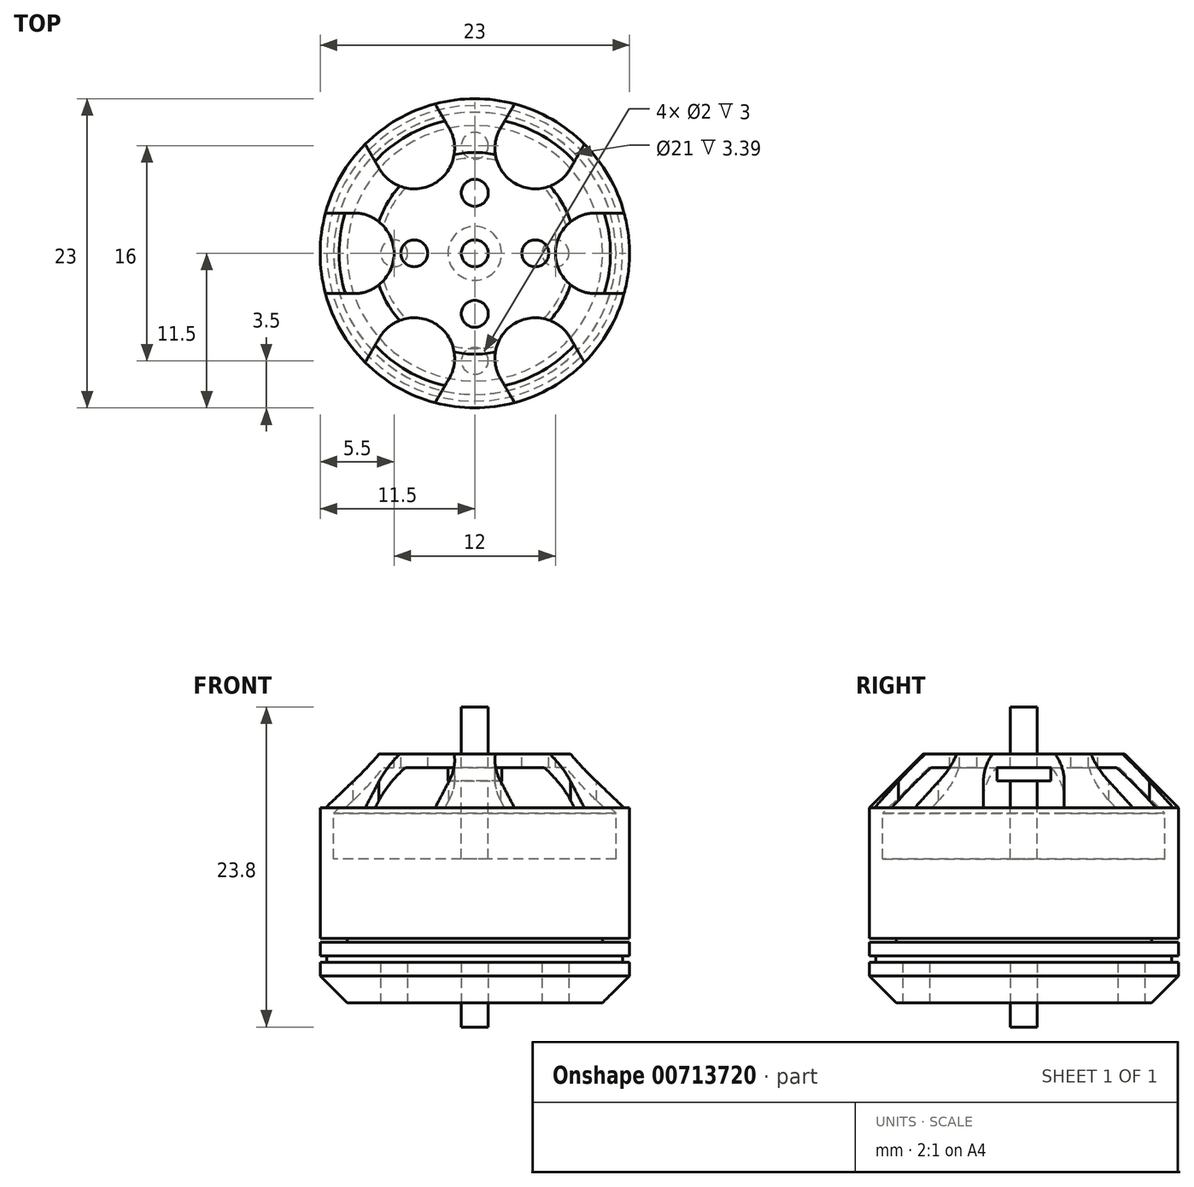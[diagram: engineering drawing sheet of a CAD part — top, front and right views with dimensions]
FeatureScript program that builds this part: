
annotation { "Feature Type Name" : "Feature", "Feature Type Description" : "" }
export const myFeature = defineFeature(function(context is Context, id is Id, definition is map)
    precondition{}
    {
        {
            var Q0;
            Q0=qCreatedBy(makeId("Front.planeOp"),FACE);
            var sketch = newSketch(context, id + "F0", { "sketchPlane" : qUnion([Q0])});
            skLineSegment(sketch, "E0", {"start": v(0, 22) * mm, "end": v(0, 0) * mm});
            skLineSegment(sketch, "E1", {"start": v(1, 0) * mm, "end": v(9.5, 0) * mm});
            skLineSegment(sketch, "E2", {"start": v(9.5, 0) * mm, "end": v(11.5, 2) * mm});
            skLineSegment(sketch, "E3", {"start": v(11.5, 2) * mm, "end": v(11.5, 3) * mm});
            skLineSegment(sketch, "E4", {"start": v(11.5, 14.5) * mm, "end": v(7.5, 18.5) * mm});
            skLineSegment(sketch, "E5", {"start": v(7.5, 18.5) * mm, "end": v(1, 18.5) * mm});
            skLineSegment(sketch, "E6", {"start": v(1, 18.5) * mm, "end": v(1, 22) * mm});
            skLineSegment(sketch, "E7", {"start": v(1, 22) * mm, "end": v(0, 22) * mm});
            skLineSegment(sketch, "E8", {"start": v(0, 0) * mm, "end": v(0, -1.8) * mm});
            skLineSegment(sketch, "E9", {"start": v(0, -1.8) * mm, "end": v(1, -1.8) * mm});
            skLineSegment(sketch, "E10", {"start": v(1, -1.8) * mm, "end": v(1, 0) * mm});
            skLineSegment(sketch, "E11", {"start": v(2, 17.5) * mm, "end": v(7.09, 17.5) * mm});
            skLineSegment(sketch, "E12", {"start": v(7.09, 17.5) * mm, "end": v(10.5, 14.09) * mm});
            skLineSegment(sketch, "E13", {"start": v(10.5, 14.09) * mm, "end": v(10.5, 10.7) * mm});
            skLineSegment(sketch, "E14", {"start": v(10.5, 10.7) * mm, "end": v(1, 10.7) * mm});
            skLineSegment(sketch, "E15", {"start": v(1, 10.7) * mm, "end": v(1, 16.5) * mm});
            skLineSegment(sketch, "E16", {"start": v(1, 16.5) * mm, "end": v(2, 16.5) * mm});
            skLineSegment(sketch, "E17", {"start": v(2, 16.5) * mm, "end": v(2, 17.5) * mm});
            skLineSegment(sketch, "E18", {"start": v(11.5, 3) * mm, "end": v(11, 3) * mm});
            skLineSegment(sketch, "E19", {"start": v(11, 3) * mm, "end": v(11, 3.5) * mm});
            skLineSegment(sketch, "E20", {"start": v(11, 3.5) * mm, "end": v(11.5, 3.5) * mm});
            skLineSegment(sketch, "E21", {"start": v(11.5, 4.5) * mm, "end": v(9.5, 4.5) * mm});
            skLineSegment(sketch, "E22", {"start": v(9.5, 4.5) * mm, "end": v(9.5, 4.8) * mm});
            skLineSegment(sketch, "E23", {"start": v(9.5, 4.8) * mm, "end": v(11.5, 4.8) * mm});
            skLineSegment(sketch, "E24.trimOffspring", {"start": v(11.5, 3.5) * mm, "end": v(11.5, 4.5) * mm});
            skLineSegment(sketch, "E25.trimOffspring", {"start": v(11.5, 4.8) * mm, "end": v(11.5, 14.5) * mm});
            skSolve(sketch);
        }
        {
            var Q0;
            Q0=makeQuery(id+"F0.imprint","IMPRINT",FACE,{"disambiguationData":[TD([[makeQuery(id+"F0.imprint","IMPRINT",EDGE,{"derivedFrom":sQuery(id+"F0.wireOp",EDGE,"E0")}),1.0]])]});
            var Q1;
            Q1=sQuery(id+"F0.wireOp",EDGE,"E0");
            revolve(context, id + "F1", {"entities" : qUnion([Q0]), "axis" : qUnion([Q1]), "revolveType" : RevolveType.FULL});
        }
        {
            var Q0;
            Q0=makeQuery(id+"F1.opRevolve","SWEPT_FACE",FACE,{"disambiguationData":[OSD([sQuery(id+"F0.wireOp",EDGE,"E5")])]});
            var sketch = newSketch(context, id + "F2", { "sketchPlane" : qUnion([Q0])});
            skCircle(sketch, "E26", {"center": v(0, 0) * mm, "radius": 4.5 * mm, "construction": true});
            skLineSegment(sketch, "E27", {"start": v(0, 0) * mm, "end": v(-9, 0) * mm, "construction": true});
            skCircle(sketch, "E28", {"center": v(4.5, 0) * mm, "radius": 1 * mm});
            skCircle(sketch, "E29.1.0", {"center": v(0, 4.5) * mm, "radius": 1 * mm});
            skCircle(sketch, "E29.2.0", {"center": v(-4.5, 0) * mm, "radius": 1 * mm});
            skCircle(sketch, "E29.3.0", {"center": v(0, -4.5) * mm, "radius": 1 * mm});
            skArc(sketch, "E30", {"start": v(-9.05, -3) * mm, "mid": v(-6, 0) * mm, "end": v(-9.05, 3) * mm});
            skLineSegment(sketch, "E31", {"start": v(-8.95, -3) * mm, "end": v(-15.53, -3) * mm});
            skLineSegment(sketch, "E32", {"start": v(-15.53, -3) * mm, "end": v(-15.53, 3) * mm});
            skLineSegment(sketch, "E33", {"start": v(-15.53, 3) * mm, "end": v(-8.95, 3) * mm});
            skLineSegment(sketch, "E34.1.0", {"start": v(-5.17, -14.95) * mm, "end": v(-10.36, -11.95) * mm});
            skLineSegment(sketch, "E34.1.1", {"start": v(-1.88, -9.25) * mm, "end": v(-5.17, -14.95) * mm});
            skArc(sketch, "E34.1.2", {"start": v(-1.93, -9.34) * mm, "mid": v(-3, -5.2) * mm, "end": v(-7.12, -6.34) * mm});
            skLineSegment(sketch, "E34.1.3", {"start": v(-10.36, -11.95) * mm, "end": v(-7.07, -6.25) * mm});
            skLineSegment(sketch, "E34.2.0", {"start": v(10.36, -11.95) * mm, "end": v(5.17, -14.95) * mm});
            skLineSegment(sketch, "E34.2.1", {"start": v(7.07, -6.25) * mm, "end": v(10.36, -11.95) * mm});
            skArc(sketch, "E34.2.2", {"start": v(7.12, -6.34) * mm, "mid": v(3, -5.2) * mm, "end": v(1.93, -9.34) * mm});
            skLineSegment(sketch, "E34.2.3", {"start": v(5.17, -14.95) * mm, "end": v(1.88, -9.25) * mm});
            skLineSegment(sketch, "E34.3.0", {"start": v(15.53, 3) * mm, "end": v(15.53, -3) * mm});
            skLineSegment(sketch, "E34.3.1", {"start": v(8.95, 3) * mm, "end": v(15.53, 3) * mm});
            skArc(sketch, "E34.3.2", {"start": v(9.05, 3) * mm, "mid": v(6, 0) * mm, "end": v(9.05, -3) * mm});
            skLineSegment(sketch, "E34.3.3", {"start": v(15.53, -3) * mm, "end": v(8.95, -3) * mm});
            skLineSegment(sketch, "E34.4.0", {"start": v(5.17, 14.95) * mm, "end": v(10.36, 11.95) * mm});
            skLineSegment(sketch, "E34.4.1", {"start": v(1.88, 9.25) * mm, "end": v(5.17, 14.95) * mm});
            skArc(sketch, "E34.4.2", {"start": v(1.93, 9.34) * mm, "mid": v(3, 5.2) * mm, "end": v(7.12, 6.34) * mm});
            skLineSegment(sketch, "E34.4.3", {"start": v(10.36, 11.95) * mm, "end": v(7.07, 6.25) * mm});
            skLineSegment(sketch, "E34.5.0", {"start": v(-10.36, 11.95) * mm, "end": v(-5.17, 14.95) * mm});
            skLineSegment(sketch, "E34.5.1", {"start": v(-7.07, 6.25) * mm, "end": v(-10.36, 11.95) * mm});
            skArc(sketch, "E34.5.2", {"start": v(-7.12, 6.34) * mm, "mid": v(-3, 5.2) * mm, "end": v(-1.93, 9.34) * mm});
            skLineSegment(sketch, "E34.5.3", {"start": v(-5.17, 14.95) * mm, "end": v(-1.88, 9.25) * mm});
            skSolve(sketch);
        }
        {
            var Q0;
            Q0=qSketchRegion(id+"F2",true);
            extrude(context, id + "F3", {"entities" : qUnion([Q0]), "operationType" : NewBodyOperationType.REMOVE, "oppositeDirection" : true, "depth" : 4 * mm});
        }
        {
            var Q0;
            Q0=makeQuery(id+"F1.opRevolve","SWEPT_FACE",FACE,{"disambiguationData":[OSD([sQuery(id+"F0.wireOp",EDGE,"E1")])]});
            var sketch = newSketch(context, id + "F4", { "sketchPlane" : qUnion([Q0])});
            skCircle(sketch, "E35", {"center": v(0, 0) * mm, "radius": 6 * mm, "construction": true});
            skCircle(sketch, "E36", {"center": v(0, 0) * mm, "radius": 8 * mm, "construction": true});
            skCircle(sketch, "E37", {"center": v(6, 0) * mm, "radius": 1 * mm});
            skCircle(sketch, "E38", {"center": v(-6, 0) * mm, "radius": 1 * mm});
            skCircle(sketch, "E39", {"center": v(0, -8) * mm, "radius": 1 * mm});
            skCircle(sketch, "E40", {"center": v(0, 8) * mm, "radius": 1 * mm});
            skSolve(sketch);
        }
        {
            var Q0;
            Q0=qSketchRegion(id+"F4",true);
            extrude(context, id + "F5", {"entities" : qUnion([Q0]), "operationType" : NewBodyOperationType.REMOVE, "oppositeDirection" : true, "depth" : 3 * mm});
        }
    });
